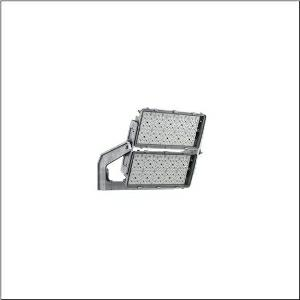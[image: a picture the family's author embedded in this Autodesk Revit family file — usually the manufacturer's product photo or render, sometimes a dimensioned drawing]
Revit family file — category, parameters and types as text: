
# Revit family: floodlight_fl_11_maxi_remote___rs07_5xa779514k01ba_6340
name_source: partatom
category: Lighting Fixtures
units: mm (PartAtom-declared; Revit-internal decimal feet)

## family parameters
Cut with Voids When Loaded = No
Host = Face
Light Source = No
Part Type = Normal
Room Calculation Point = No
Round Connector Dimension = Use Diameter
Shared = No

## types (1)
- --- (1 x LED, 75300 lm, 707.9 W, 5700K)
    Apparent Load = 708 VA
    CIE Flux Codes = 80 93 99 100 99
    Color Rendering = 90
    Color Temperature = 5700K
    Default Elevation = 1800 mm
    Description = Floodlight FL 11  maxi  Remote floodlight; light control with lens of PMMA; cover panel of toughened safety glass, transparent; light distribution: RS07, rotationally symmetric direct distribution, LEDcolour temperature: 5700K, rated luminous flux: 75.300lm, colour rendering: CRI > 90, light colour: 957; luminous efficacy: 106lm/W; brightness control: DMX+RDM; with terminal, 8-pole, max. 2.5mm², mains connection: 220..240V/380..400V AC, 50/60Hz, surge voltage resistance: line to ground: 10kV, ECG replaceable separately, LED unit replaceable without ESD environment, dustproof LED module, dimming range 10..100%; 708W floodlight with 2x LED unit of diecast aluminium, coated grey; length: 713mm / width: 651mm / height: 338mm; housing frame, of diecast aluminium, uncoated, natural, mounting bracket, of diecast aluminium, uncoated, natural, equipment: Longlife, protection rating (complete): IP66; insulation class (complete): insulation class I (protective earthing); certification: CE, ENEC, VDE; ball protection: ball impact resistance with accessories, only for outdoor installations, rated ambient temperature 10°C, permissible operating ambient temperature: -40..+40°C, permissible storage temperature: -40..+85°C; packaging unit: 1 piece

Light Distribution: RS07
    Height = 320 mm
    Lamp = 1 x LED
    Lamp Light Flux = 75300 lm
    Lamp Power = 707.9 W
    Lamp count = 1
    Length = 712 mm
    Luminous efficacy = 106 lm/W
    Manufacturer = Siteco
    ModVariant = No
    Model = 5XA779514K01BA
    Number of Poles = 1
    OnlyDefault = Yes
    Power Factor = 1
    Product Name = Floodlight FL 11 maxi Remote | RS07
    Product group = floodlight | pylon top
    ProductGroupID = 6101
    Protection Class = Protection class I
    Protection Degree = IP 66
    RLX_Detail_Level = 1
    RlxData = <blob elided: 41133 chars, md5=2998cf9b>
    Socket = socket
    Standby Power = 0 W
    System Light Flux = 75300 lm
    System Power = 708 W
    Type Comments = factory setting: luminous flux: 100 % | dim-lin: 254 | 740 mA
    Type Image = l_1006788.jpg
    URL = http://relux.com
    VarID = @adj_095049
    Voltage = 0 V
    Weight = 0.00 kg
    Width = 655 mm

## geometry (parser evidence)
native form markers: Blend x4, Sweep x12
no freeform markers — native parametric forms only
